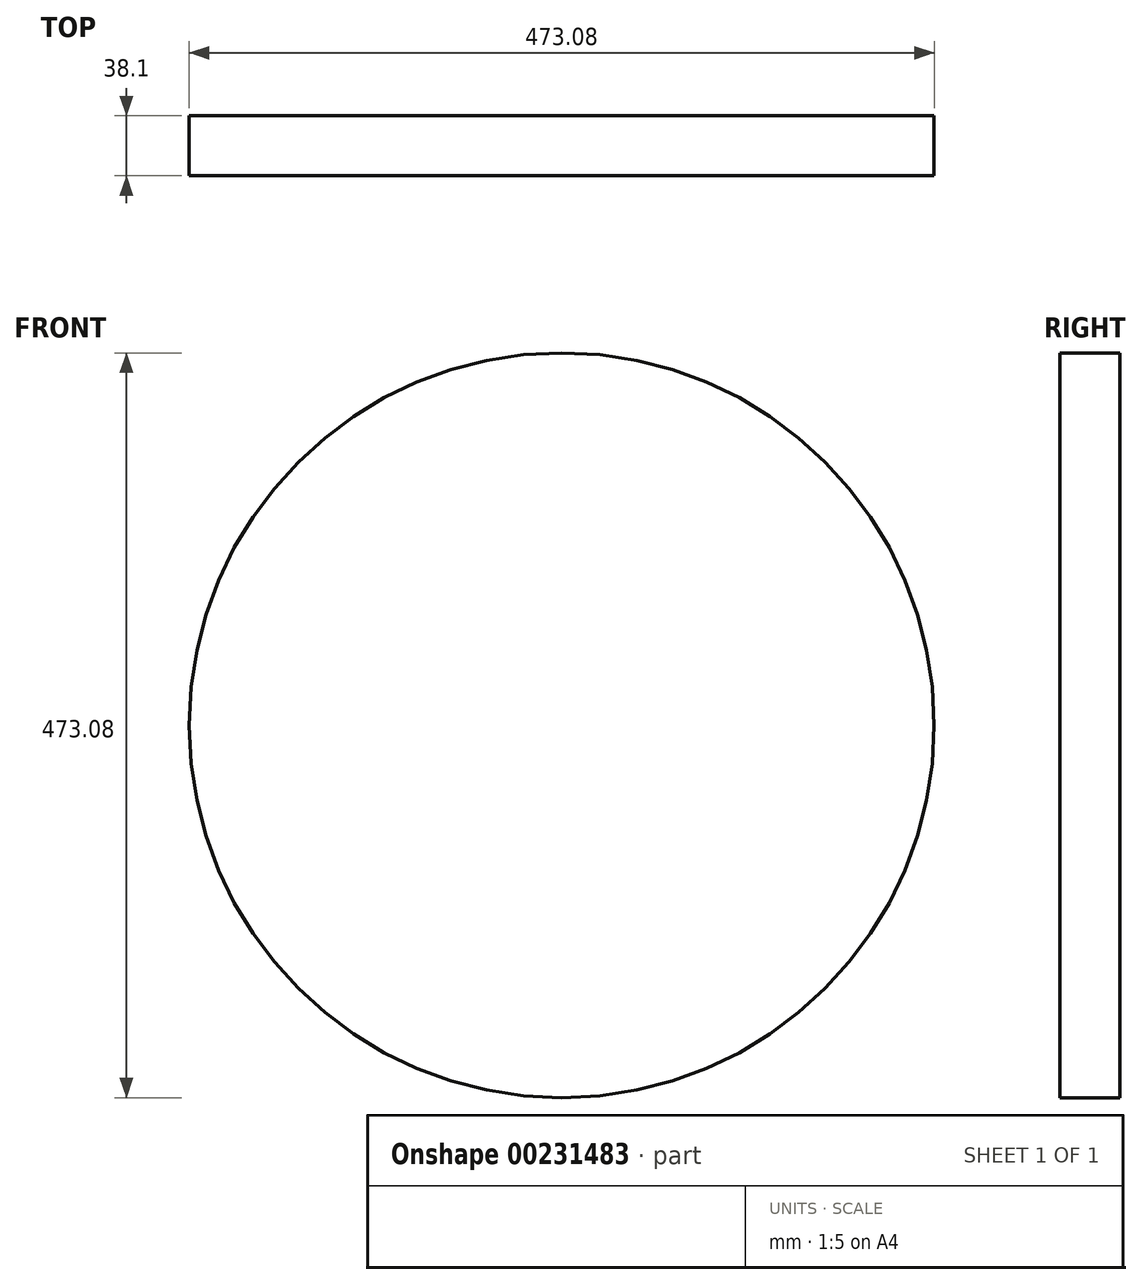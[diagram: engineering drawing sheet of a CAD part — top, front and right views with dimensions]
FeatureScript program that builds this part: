
annotation { "Feature Type Name" : "Feature", "Feature Type Description" : "" }
export const myFeature = defineFeature(function(context is Context, id is Id, definition is map)
    precondition{}
    {
        {
            var Q0;
            Q0=qCreatedBy(makeId("Front.planeOp"),FACE);
            var sketch = newSketch(context, id + "F0", { "sketchPlane" : qUnion([Q0])});
            skCircle(sketch, "E0", {"center": v(0, 0) * mm, "radius": 236.54 * mm});
            skSolve(sketch);
        }
        {
            var Q0;
            Q0 = qSketchRegion(id + "F0", true);
            extrude(context, id + "F1", {"entities" : qUnion([Q0]), "depth" : 38.1 * mm});
        }
    });
